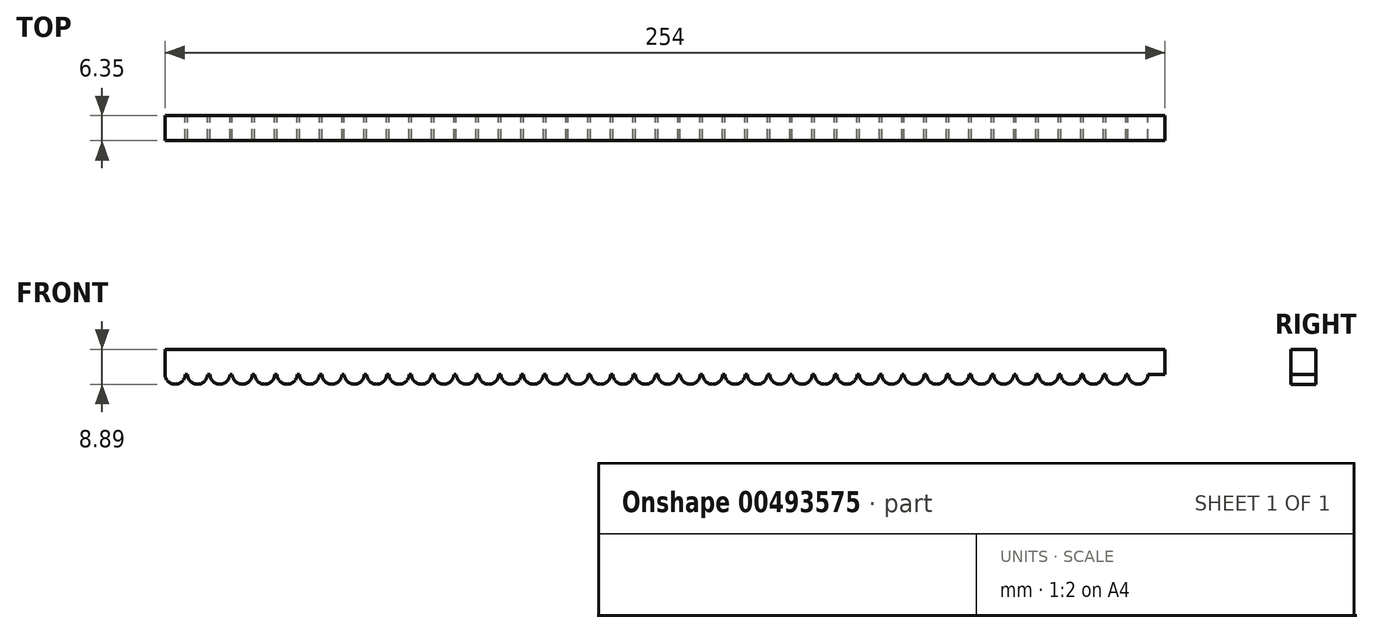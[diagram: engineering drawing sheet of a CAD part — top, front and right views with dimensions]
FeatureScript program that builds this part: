
annotation { "Feature Type Name" : "Feature", "Feature Type Description" : "" }
export const myFeature = defineFeature(function(context is Context, id is Id, definition is map)
    precondition{}
    {
        {
            var Q0;
            Q0=qCreatedBy(makeId("Front.planeOp"),FACE);
            var sketch = newSketch(context, id + "F0", { "sketchPlane" : qUnion([Q0])});
            skLineSegment(sketch, "E0.top", {"start": v(0, 6.35) * mm, "end": v(254, 6.35) * mm});
            skLineSegment(sketch, "E0.left", {"start": v(0, 0) * mm, "end": v(0, 6.35) * mm});
            skLineSegment(sketch, "E0.right", {"start": v(254, 0) * mm, "end": v(254, 6.35) * mm});
            skArc(sketch, "E1", {"start": v(0, 0) * mm, "mid": v(2.54, -2.54) * mm, "end": v(5.08, 0) * mm});
            skArc(sketch, "E2.1.0.0", {"start": v(5.69, 0) * mm, "mid": v(8.23, -2.54) * mm, "end": v(10.77, 0) * mm});
            skArc(sketch, "E2.2.0.0", {"start": v(11.38, 0) * mm, "mid": v(13.92, -2.54) * mm, "end": v(16.46, 0) * mm});
            skArc(sketch, "E2.3.0.0", {"start": v(17.07, 0) * mm, "mid": v(19.6, -2.54) * mm, "end": v(22.15, 0) * mm});
            skArc(sketch, "E2.4.0.0", {"start": v(22.76, 0) * mm, "mid": v(25.3, -2.54) * mm, "end": v(27.84, 0) * mm});
            skArc(sketch, "E2.5.0.0", {"start": v(28.45, 0) * mm, "mid": v(30.99, -2.54) * mm, "end": v(33.53, 0) * mm});
            skArc(sketch, "E2.6.0.0", {"start": v(34.14, 0) * mm, "mid": v(36.68, -2.54) * mm, "end": v(39.22, 0) * mm});
            skArc(sketch, "E2.7.0.0", {"start": v(39.83, 0) * mm, "mid": v(42.37, -2.54) * mm, "end": v(44.9, 0) * mm});
            skArc(sketch, "E2.8.0.0", {"start": v(45.52, 0) * mm, "mid": v(48.06, -2.54) * mm, "end": v(50.6, 0) * mm});
            skArc(sketch, "E2.9.0.0", {"start": v(51.2, 0) * mm, "mid": v(53.75, -2.54) * mm, "end": v(56.29, 0) * mm});
            skArc(sketch, "E2.10.0.0", {"start": v(56.9, 0) * mm, "mid": v(59.44, -2.54) * mm, "end": v(61.98, 0) * mm});
            skArc(sketch, "E2.11.0.0", {"start": v(62.59, 0) * mm, "mid": v(65.13, -2.54) * mm, "end": v(67.67, 0) * mm});
            skArc(sketch, "E2.12.0.0", {"start": v(68.28, 0) * mm, "mid": v(70.82, -2.54) * mm, "end": v(73.36, 0) * mm});
            skArc(sketch, "E2.13.0.0", {"start": v(73.96, 0) * mm, "mid": v(76.5, -2.54) * mm, "end": v(79.04, 0) * mm});
            skArc(sketch, "E2.14.0.0", {"start": v(79.65, 0) * mm, "mid": v(82.2, -2.54) * mm, "end": v(84.73, 0) * mm});
            skArc(sketch, "E2.15.0.0", {"start": v(85.34, 0) * mm, "mid": v(87.88, -2.54) * mm, "end": v(90.42, 0) * mm});
            skArc(sketch, "E2.16.0.0", {"start": v(91.03, 0) * mm, "mid": v(93.57, -2.54) * mm, "end": v(96.11, 0) * mm});
            skArc(sketch, "E2.17.0.0", {"start": v(96.72, 0) * mm, "mid": v(99.26, -2.54) * mm, "end": v(101.8, 0) * mm});
            skArc(sketch, "E2.18.0.0", {"start": v(102.41, 0) * mm, "mid": v(104.95, -2.54) * mm, "end": v(107.5, 0) * mm});
            skArc(sketch, "E2.19.0.0", {"start": v(108.1, 0) * mm, "mid": v(110.64, -2.54) * mm, "end": v(113.18, 0) * mm});
            skArc(sketch, "E2.20.0.0", {"start": v(113.8, 0) * mm, "mid": v(116.33, -2.54) * mm, "end": v(118.87, 0) * mm});
            skArc(sketch, "E2.21.0.0", {"start": v(119.48, 0) * mm, "mid": v(122.02, -2.54) * mm, "end": v(124.56, 0) * mm});
            skArc(sketch, "E2.22.0.0", {"start": v(125.17, 0) * mm, "mid": v(127.71, -2.54) * mm, "end": v(130.25, 0) * mm});
            skArc(sketch, "E2.23.0.0", {"start": v(130.86, 0) * mm, "mid": v(133.4, -2.54) * mm, "end": v(135.94, 0) * mm});
            skArc(sketch, "E2.24.0.0", {"start": v(136.55, 0) * mm, "mid": v(139.1, -2.54) * mm, "end": v(141.63, 0) * mm});
            skArc(sketch, "E2.25.0.0", {"start": v(142.24, 0) * mm, "mid": v(144.78, -2.54) * mm, "end": v(147.32, 0) * mm});
            skArc(sketch, "E2.26.0.0", {"start": v(147.93, 0) * mm, "mid": v(150.47, -2.54) * mm, "end": v(153, 0) * mm});
            skArc(sketch, "E2.27.0.0", {"start": v(153.62, 0) * mm, "mid": v(156.16, -2.54) * mm, "end": v(158.7, 0) * mm});
            skArc(sketch, "E2.28.0.0", {"start": v(159.3, 0) * mm, "mid": v(161.85, -2.54) * mm, "end": v(164.39, 0) * mm});
            skArc(sketch, "E2.29.0.0", {"start": v(165, 0) * mm, "mid": v(167.54, -2.54) * mm, "end": v(170.08, 0) * mm});
            skArc(sketch, "E2.30.0.0", {"start": v(170.69, 0) * mm, "mid": v(173.23, -2.54) * mm, "end": v(175.77, 0) * mm});
            skArc(sketch, "E2.31.0.0", {"start": v(176.38, 0) * mm, "mid": v(178.92, -2.54) * mm, "end": v(181.46, 0) * mm});
            skArc(sketch, "E2.32.0.0", {"start": v(182.07, 0) * mm, "mid": v(184.6, -2.54) * mm, "end": v(187.15, 0) * mm});
            skArc(sketch, "E2.33.0.0", {"start": v(187.76, 0) * mm, "mid": v(190.3, -2.54) * mm, "end": v(192.84, 0) * mm});
            skArc(sketch, "E2.34.0.0", {"start": v(193.45, 0) * mm, "mid": v(195.99, -2.54) * mm, "end": v(198.53, 0) * mm});
            skArc(sketch, "E2.35.0.0", {"start": v(199.14, 0) * mm, "mid": v(201.68, -2.54) * mm, "end": v(204.22, 0) * mm});
            skArc(sketch, "E2.36.0.0", {"start": v(204.83, 0) * mm, "mid": v(207.37, -2.54) * mm, "end": v(209.9, 0) * mm});
            skArc(sketch, "E2.37.0.0", {"start": v(210.52, 0) * mm, "mid": v(213.06, -2.54) * mm, "end": v(215.6, 0) * mm});
            skArc(sketch, "E2.38.0.0", {"start": v(216.2, 0) * mm, "mid": v(218.74, -2.54) * mm, "end": v(221.28, 0) * mm});
            skArc(sketch, "E2.39.0.0", {"start": v(221.9, 0) * mm, "mid": v(224.43, -2.54) * mm, "end": v(226.97, 0) * mm});
            skArc(sketch, "E2.40.0.0", {"start": v(227.58, 0) * mm, "mid": v(230.12, -2.54) * mm, "end": v(232.66, 0) * mm});
            skArc(sketch, "E2.41.0.0", {"start": v(233.27, 0) * mm, "mid": v(235.81, -2.54) * mm, "end": v(238.35, 0) * mm});
            skArc(sketch, "E2.42.0.0", {"start": v(238.96, 0) * mm, "mid": v(241.5, -2.54) * mm, "end": v(244.04, 0) * mm});
            skArc(sketch, "E2.43.0.0", {"start": v(244.65, 0) * mm, "mid": v(247.2, -2.54) * mm, "end": v(249.73, 0) * mm});
            skLineSegment(sketch, "E2.direction1", {"start": v(5.08, 0) * mm, "end": v(5.69, 0) * mm, "construction": true});
            skLineSegment(sketch, "E3.trimOffspring", {"start": v(10.77, 0) * mm, "end": v(11.38, 0) * mm});
            skLineSegment(sketch, "E4.trimOffspring", {"start": v(16.46, 0) * mm, "end": v(17.07, 0) * mm});
            skLineSegment(sketch, "E5.trimOffspring", {"start": v(22.15, 0) * mm, "end": v(22.76, 0) * mm});
            skLineSegment(sketch, "E6.trimOffspring", {"start": v(27.84, 0) * mm, "end": v(28.45, 0) * mm});
            skLineSegment(sketch, "E7.trimOffspring", {"start": v(33.53, 0) * mm, "end": v(34.14, 0) * mm});
            skLineSegment(sketch, "E8.trimOffspring", {"start": v(39.22, 0) * mm, "end": v(39.83, 0) * mm});
            skLineSegment(sketch, "E9.trimOffspring", {"start": v(44.9, 0) * mm, "end": v(45.52, 0) * mm});
            skLineSegment(sketch, "E10.trimOffspring", {"start": v(50.6, 0) * mm, "end": v(51.2, 0) * mm});
            skLineSegment(sketch, "E11.trimOffspring", {"start": v(61.98, 0) * mm, "end": v(62.59, 0) * mm});
            skLineSegment(sketch, "E12.trimOffspring", {"start": v(67.67, 0) * mm, "end": v(68.28, 0) * mm});
            skLineSegment(sketch, "E13.trimOffspring", {"start": v(73.36, 0) * mm, "end": v(73.96, 0) * mm});
            skLineSegment(sketch, "E14.trimOffspring", {"start": v(79.04, 0) * mm, "end": v(79.65, 0) * mm});
            skLineSegment(sketch, "E15.trimOffspring", {"start": v(84.73, 0) * mm, "end": v(85.34, 0) * mm});
            skLineSegment(sketch, "E16.trimOffspring", {"start": v(90.42, 0) * mm, "end": v(91.03, 0) * mm});
            skLineSegment(sketch, "E17.trimOffspring", {"start": v(101.8, 0) * mm, "end": v(102.41, 0) * mm});
            skLineSegment(sketch, "E18.trimOffspring", {"start": v(113.18, 0) * mm, "end": v(113.8, 0) * mm});
            skLineSegment(sketch, "E19.trimOffspring", {"start": v(118.87, 0) * mm, "end": v(119.48, 0) * mm});
            skLineSegment(sketch, "E20.trimOffspring", {"start": v(107.5, 0) * mm, "end": v(108.1, 0) * mm});
            skLineSegment(sketch, "E21.trimOffspring", {"start": v(124.56, 0) * mm, "end": v(125.17, 0) * mm});
            skLineSegment(sketch, "E22.trimOffspring", {"start": v(130.25, 0) * mm, "end": v(130.86, 0) * mm});
            skLineSegment(sketch, "E23.trimOffspring", {"start": v(141.63, 0) * mm, "end": v(142.24, 0) * mm});
            skLineSegment(sketch, "E24.trimOffspring", {"start": v(153, 0) * mm, "end": v(153.62, 0) * mm});
            skLineSegment(sketch, "E25.trimOffspring", {"start": v(147.32, 0) * mm, "end": v(147.93, 0) * mm});
            skLineSegment(sketch, "E26.trimOffspring", {"start": v(158.7, 0) * mm, "end": v(159.3, 0) * mm});
            skLineSegment(sketch, "E27.trimOffspring", {"start": v(175.77, 0) * mm, "end": v(176.38, 0) * mm});
            skLineSegment(sketch, "E28.trimOffspring", {"start": v(181.46, 0) * mm, "end": v(182.07, 0) * mm});
            skLineSegment(sketch, "E29.trimOffspring", {"start": v(187.15, 0) * mm, "end": v(187.76, 0) * mm});
            skLineSegment(sketch, "E30.trimOffspring", {"start": v(192.84, 0) * mm, "end": v(193.45, 0) * mm});
            skLineSegment(sketch, "E31.trimOffspring", {"start": v(198.53, 0) * mm, "end": v(199.14, 0) * mm});
            skLineSegment(sketch, "E32.trimOffspring", {"start": v(204.22, 0) * mm, "end": v(204.83, 0) * mm});
            skLineSegment(sketch, "E33.trimOffspring", {"start": v(209.9, 0) * mm, "end": v(210.52, 0) * mm});
            skLineSegment(sketch, "E34.trimOffspring", {"start": v(215.6, 0) * mm, "end": v(216.2, 0) * mm});
            skLineSegment(sketch, "E35.trimOffspring", {"start": v(221.28, 0) * mm, "end": v(221.9, 0) * mm});
            skLineSegment(sketch, "E36.trimOffspring", {"start": v(226.97, 0) * mm, "end": v(227.58, 0) * mm});
            skLineSegment(sketch, "E37.trimOffspring", {"start": v(232.66, 0) * mm, "end": v(233.27, 0) * mm});
            skLineSegment(sketch, "E38.trimOffspring", {"start": v(238.35, 0) * mm, "end": v(238.96, 0) * mm});
            skLineSegment(sketch, "E39.trimOffspring", {"start": v(244.04, 0) * mm, "end": v(244.65, 0) * mm});
            skLineSegment(sketch, "E40.trimOffspring", {"start": v(249.73, 0) * mm, "end": v(254, 0) * mm});
            skLineSegment(sketch, "E41", {"start": v(96.11, 0) * mm, "end": v(96.72, 0) * mm});
            skLineSegment(sketch, "E42", {"start": v(164.39, 0) * mm, "end": v(165, 0) * mm});
            skLineSegment(sketch, "E43", {"start": v(170.08, 0) * mm, "end": v(170.69, 0) * mm});
            skLineSegment(sketch, "E44", {"start": v(5.08, 0) * mm, "end": v(5.69, 0) * mm});
            skLineSegment(sketch, "E45", {"start": v(135.94, 0) * mm, "end": v(136.55, 0) * mm});
            skLineSegment(sketch, "E46", {"start": v(56.29, 0) * mm, "end": v(56.9, 0) * mm});
            skSolve(sketch);
        }
        {
            var Q0;
            Q0 = qSketchRegion(id + "F0", true);
            extrude(context, id + "F1", {"entities" : qUnion([Q0]), "depth" : 6.35 * mm, "offsetDistance" : 25.4 * mm});
        }
    });
